# Revit family: Regadera H-3010
name_source: partatom
category: Plumbing Fixtures
revit_build: Autodesk Revit 2015 (Build: 20140223_1515(x64)
units: mm (PartAtom-declared; Revit-internal decimal feet)

## types (1)
- H-3010
    Brass Chromed = Brass
    Default Elevation = 1"
    Description = Regadera de Plato Ancho de 12" Chorro Fijo con Sistema Anticalcareo
    Garantía = El producto HELVEX esta garantizado como libre de defectos en materiales y procesos de
fabricacion. El producto HELVEX esta garantizado, en lo que
se refiere a los acabados; por un periodo de 10 años en los acabados cromo y duravex, y por 2
años en cabados diferentes al cromo, a partir de la fecha de compra indicada en la factura.
    Inlet Threads = ½" - 14 NPT
    Manufacturer = HELVEX S.A. de C.V.
    Max. Water Flow = 2.2 gal/min
    Max. Working Pressure = 85.3 psi
    Min. Working Pressure = 14.2 psi
    Model = H-3010
    Type Comments = Regadera de Plato Ancho de 12"
    Type Image = H-3010.jpg

## geometry (parser evidence)
native form markers: Sweep x3
no freeform markers — native parametric forms only
